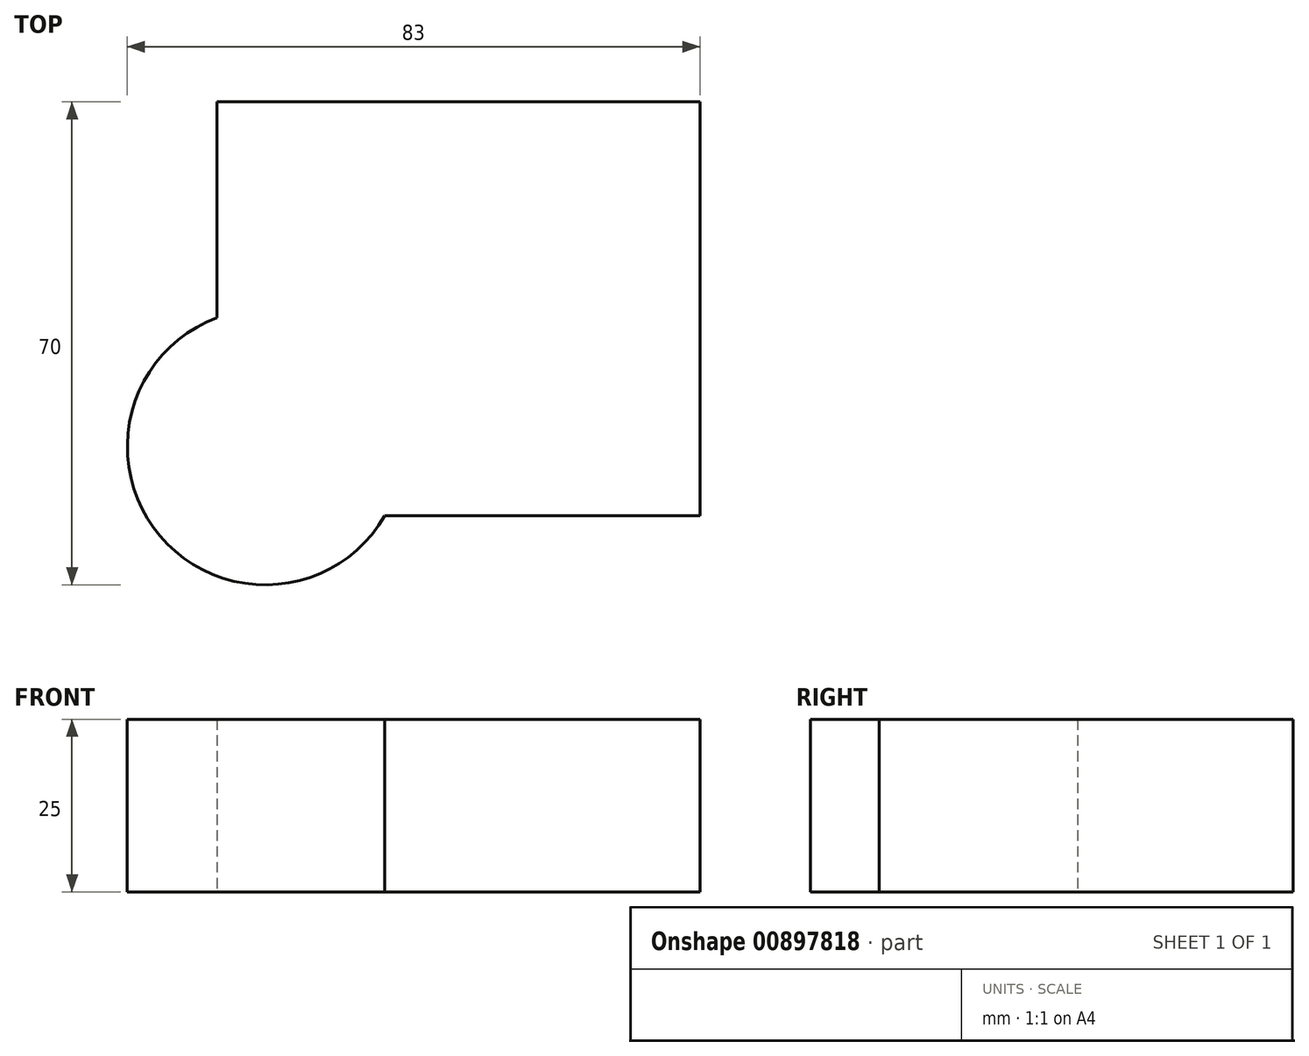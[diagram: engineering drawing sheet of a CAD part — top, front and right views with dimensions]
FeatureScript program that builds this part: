
annotation { "Feature Type Name" : "Feature", "Feature Type Description" : "" }
export const myFeature = defineFeature(function(context is Context, id is Id, definition is map)
    precondition{}
    {
        {
            var Q0;
            Q0=qCreatedBy(makeId("Top.planeOp"),FACE);
            var sketch = newSketch(context, id + "F0", { "sketchPlane" : qUnion([Q0])});
            skLineSegment(sketch, "E0.bottom", {"start": v(-50, -40) * mm, "end": v(20, -40) * mm});
            skLineSegment(sketch, "E0.top", {"start": v(-50, 20) * mm, "end": v(20, 20) * mm});
            skLineSegment(sketch, "E0.left", {"start": v(-50, -40) * mm, "end": v(-50, 20) * mm});
            skLineSegment(sketch, "E0.right", {"start": v(20, -40) * mm, "end": v(20, 20) * mm});
            skCircle(sketch, "E1", {"center": v(-43, -30) * mm, "radius": 20 * mm});
            skSolve(sketch);
        }
        {
            var Q0;
            Q0 = qSketchRegion(id + "F0", true);
            extrude(context, id + "F1", {"entities" : qUnion([Q0]), "depth" : 25 * mm, "offsetDistance" : 25 * mm});
        }
    });
